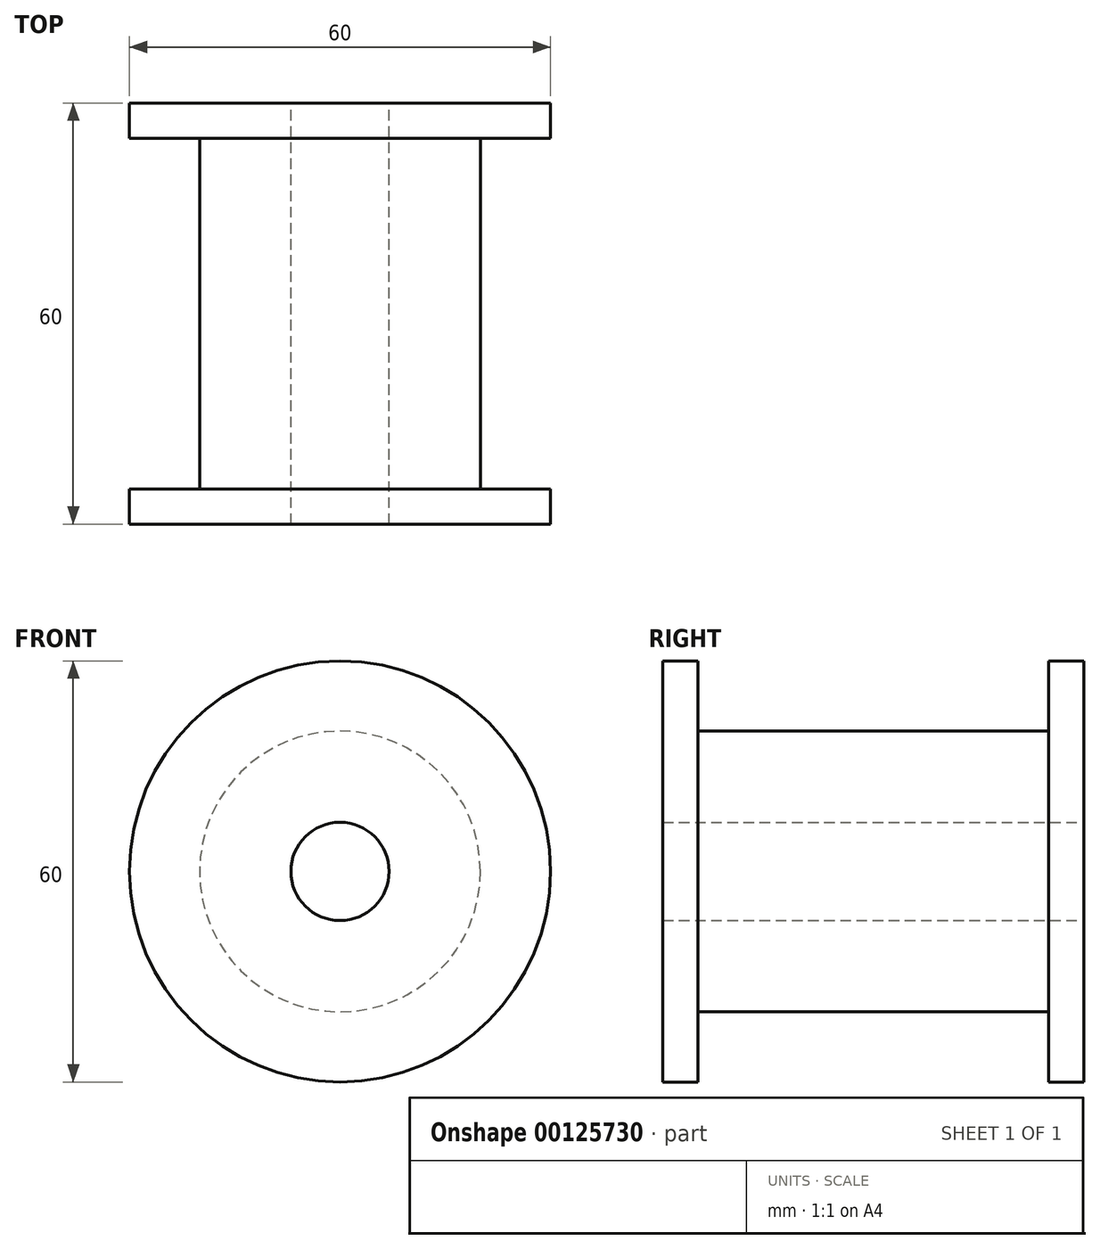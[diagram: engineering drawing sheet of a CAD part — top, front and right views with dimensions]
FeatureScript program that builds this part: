
annotation { "Feature Type Name" : "Feature", "Feature Type Description" : "" }
export const myFeature = defineFeature(function(context is Context, id is Id, definition is map)
    precondition{}
    {
        {
            var Q0;
            Q0=qCreatedBy(makeId("Front.planeOp"),FACE);
            var sketch = newSketch(context, id + "F0", { "sketchPlane" : qUnion([Q0])});
            skCircle(sketch, "E0", {"center": v(0, 0) * mm, "radius": 7 * mm});
            skCircle(sketch, "E1", {"center": v(0, 0) * mm, "radius": 20 * mm});
            skSolve(sketch);
        }
        {
            var Q0;
            Q0 = qSketchRegion(id + "F0", true);
            extrude(context, id + "F1", {"entities" : qUnion([Q0]), "depth" : 50 * mm, "symmetric" : true});
        }
        {
            var Q0;
            Q0=makeQuery(id+"F1.opExtrude","CAP_FACE",FACE,{"disambiguationData":[OSD([sQuery(id+"F0.wireOp",EDGE,"E0"),sQuery(id+"F0.wireOp",EDGE,"E1")])],"isStart":false});
            var sketch = newSketch(context, id + "F2", { "sketchPlane" : qUnion([Q0])});
            skCircle(sketch, "E2", {"center": v(0, 0) * mm, "radius": 30 * mm});
            skCircle(sketch, "E3.0", {"center": v(0, 0) * mm, "radius": 7 * mm});
            skPoint(sketch, "E4", {"position": v(-30, 0) * mm});
            skPoint(sketch, "E5", {"position": v(-20, 0) * mm});
            skSolve(sketch);
        }
        {
            var Q0;
            Q0 = qSketchRegion(id + "F2", true);
            extrude(context, id + "F3", {"entities" : qUnion([Q0]), "depth" : 5 * mm});
        }
        {
            var Q0;
            Q0=makeQuery(id+"F3.opExtrude","SWEPT_BODY",BODY,{"disambiguationData":[OSD([sQuery(id+"F2.wireOp",EDGE,"E2"),sQuery(id+"F2.wireOp",EDGE,"E3.0")])]});
            var Q1;
            Q1=qCreatedBy(makeId("Front.planeOp"),FACE);
            mirror(context, id + "F4", {"operationType" : NewBodyOperationType.ADD, "entities" : qUnion([Q0]), "mirrorPlane" : qUnion([Q1])});
        }
    });
